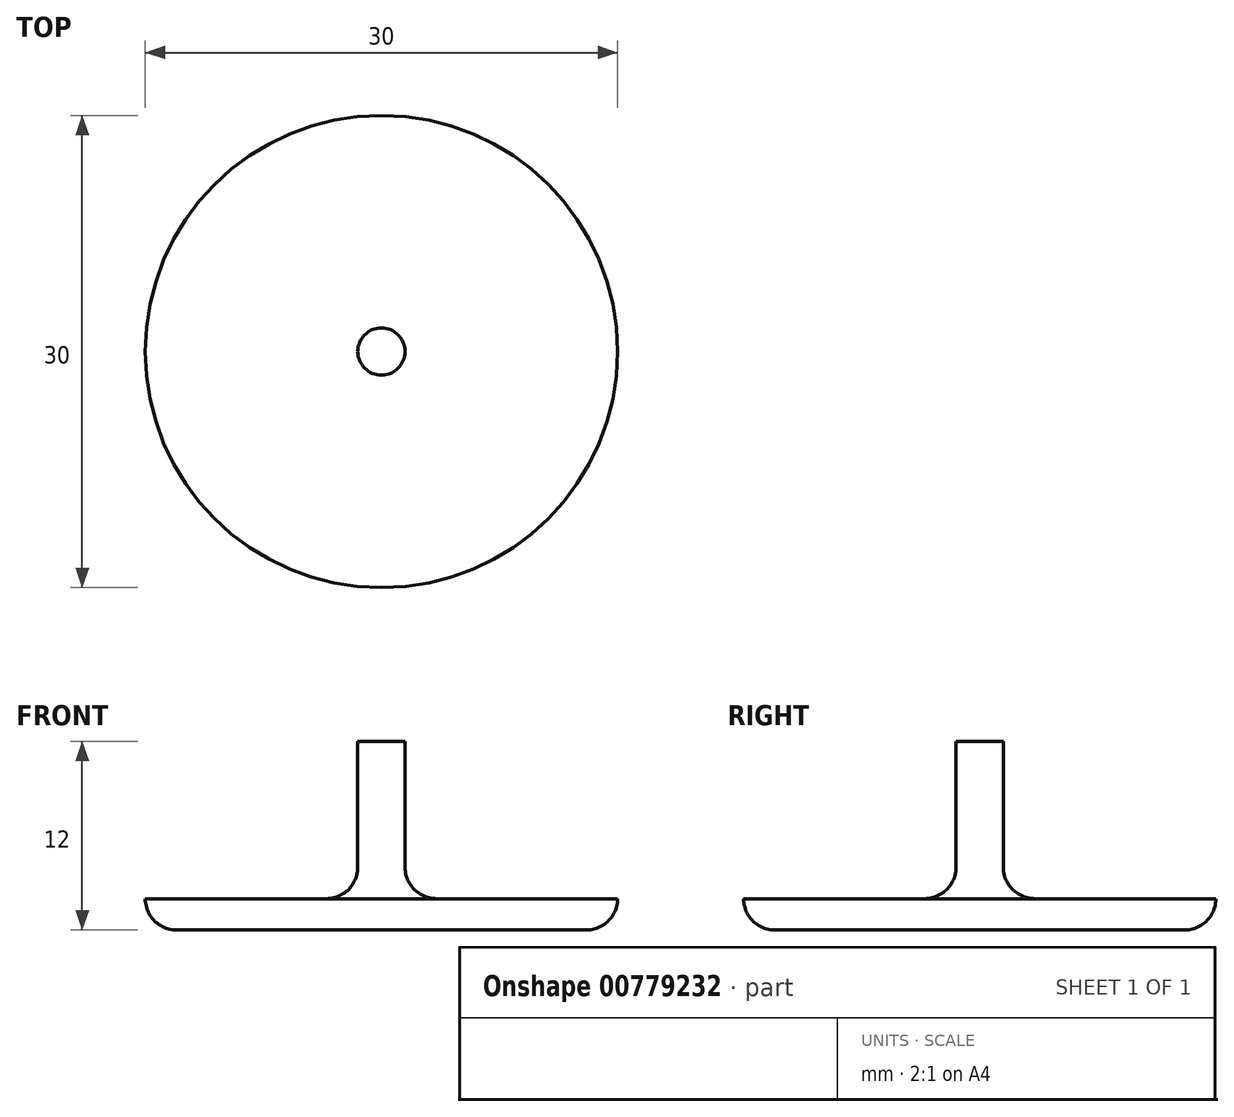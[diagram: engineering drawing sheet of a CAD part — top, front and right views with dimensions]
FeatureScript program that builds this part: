
annotation { "Feature Type Name" : "Feature", "Feature Type Description" : "" }
export const myFeature = defineFeature(function(context is Context, id is Id, definition is map)
    precondition{}
    {
        {
            var Q0;
            Q0=qCreatedBy(makeId("Front.planeOp"),FACE);
            var sketch = newSketch(context, id + "F0", { "sketchPlane" : qUnion([Q0])});
            skLineSegment(sketch, "E0.bottom", {"start": v(0, 0) * mm, "end": v(-15, 0) * mm});
            skLineSegment(sketch, "E0.top", {"start": v(0, 2) * mm, "end": v(-15, 2) * mm});
            skLineSegment(sketch, "E0.left", {"start": v(0, 0) * mm, "end": v(0, 2) * mm});
            skLineSegment(sketch, "E0.right", {"start": v(-15, 0) * mm, "end": v(-15, 2) * mm});
            skLineSegment(sketch, "E1.bottom", {"start": v(0, 2) * mm, "end": v(-1.5, 2) * mm});
            skLineSegment(sketch, "E1.left", {"start": v(0, 2) * mm, "end": v(0, 12) * mm});
            skLineSegment(sketch, "E1.right", {"start": v(-1.5, 2) * mm, "end": v(-1.5, 12) * mm});
            skLineSegment(sketch, "E2", {"start": v(0, 12) * mm, "end": v(-1.5, 12) * mm});
            skLineSegment(sketch, "E3", {"start": v(0, 0) * mm, "end": v(0, 55.48) * mm, "construction": true});
            skFitSpline(sketch, "E4", {"points": [v(0, 12) * mm, v(-3, 13.31) * mm, v(-4.94, 15.07) * mm, v(-5.38, 19.39) * mm], "startDerivative": vector(-9.53, 3.77) * mm, "endDerivative": vector(0.27, 12.88) * mm});
            skSolve(sketch);
        }
        {
            var Q0;
            Q0=makeQuery(id+"F0.imprint","IMPRINT",FACE,{"disambiguationData":[TD([[makeQuery(id+"F0.imprint","IMPRINT",EDGE,{"derivedFrom":sQuery(id+"F0.wireOp",EDGE,"E2")}),-1.0]])]});
            var Q1;
            Q1=makeQuery(id+"F0.imprint","IMPRINT",FACE,{"disambiguationData":[TD([[makeQuery(id+"F0.imprint","IMPRINT",EDGE,{"derivedFrom":sQuery(id+"F0.wireOp",EDGE,"E0.bottom")}),-1.0]])]});
            var Q2;
            {var subQ2=sQuery(id+"F0.wireOp",EDGE,"E1.left");Q2=makeQuery(id+"F0.imprint","IMPRINT",FACE,{"disambiguationData":[TD([[makeQuery(id+"F0.imprint","IMPRINT",EDGE,{"derivedFrom":subQ2}),1.0]])]});}
            var Q3;
            Q3=sQuery(id+"F0.wireOp",EDGE,"E3");
            revolve(context, id + "F1", {"surfaceOperationType" : NewSurfaceOperationType.NEW, "entities" : qUnion([Q0, Q1, Q2]), "axis" : qUnion([Q3]), "revolveType" : RevolveType.FULL});
        }
        {
            var Q0;
            Q0=makeQuery(id+"F1.opRevolve","SWEPT_EDGE",EDGE,{"disambiguationData":[OSD([sQuery(id+"F0.wireOp",EDGE,"E0.bottom"),sQuery(id+"F0.wireOp",EDGE,"E0.right")])]});
            var Q1;
            Q1=makeQuery(id+"F1.opRevolve","SWEPT_EDGE",EDGE,{"disambiguationData":[OSD([sQuery(id+"F0.wireOp",EDGE,"E0.top"),sQuery(id+"F0.wireOp",EDGE,"E1.right")])]});
            fillet(context, id + "F2", {"entities" : qUnion([Q0, Q1]), "radius" : 2 * mm, "tangentPropagation" : true, "allowEdgeOverflow" : false});
        }
    });
